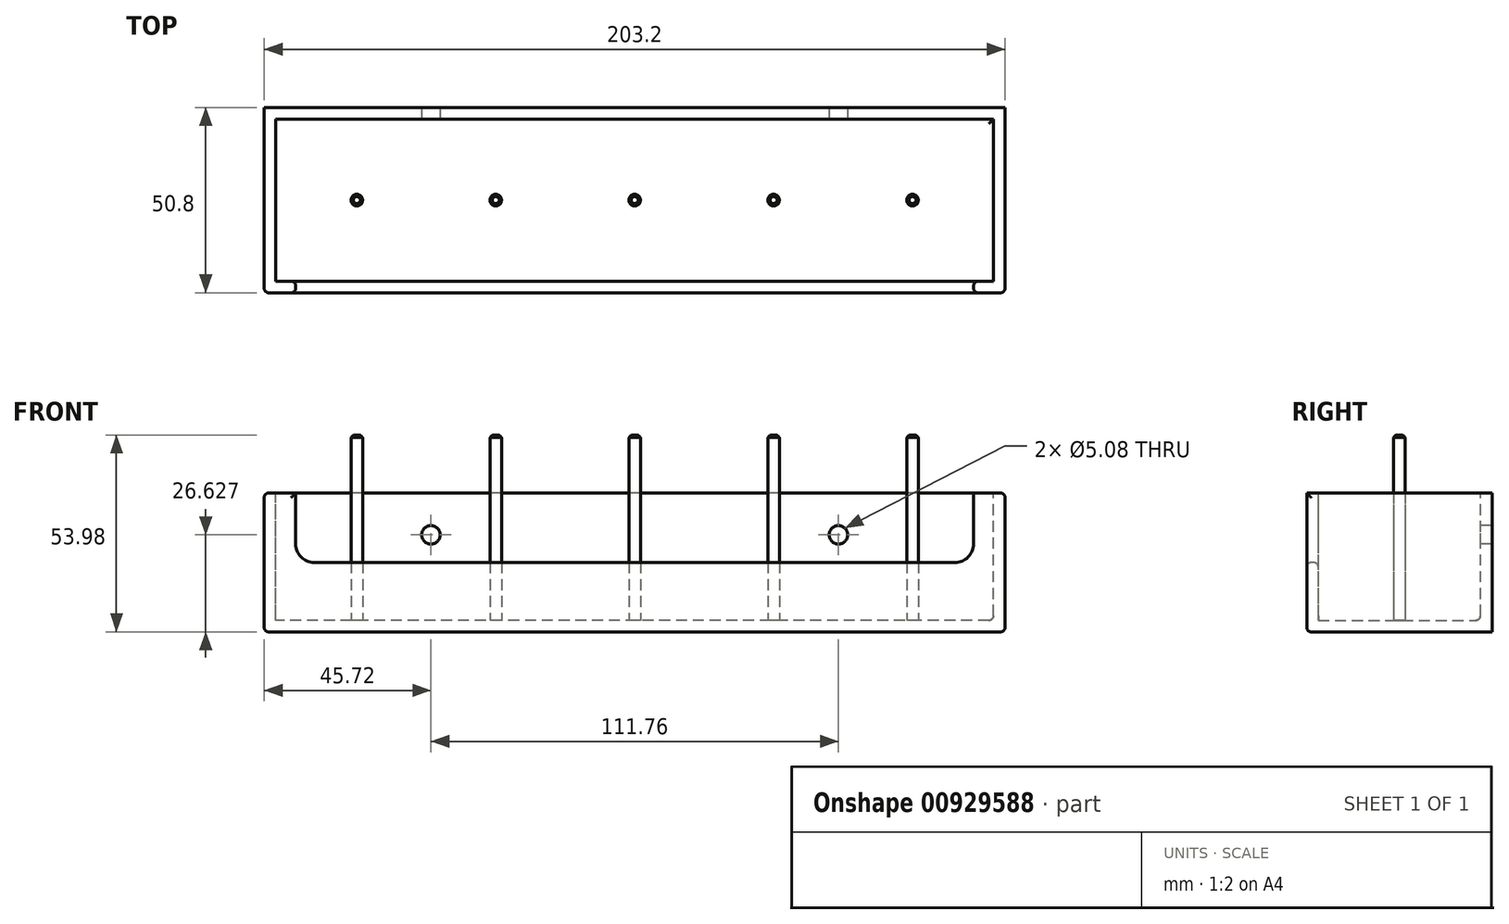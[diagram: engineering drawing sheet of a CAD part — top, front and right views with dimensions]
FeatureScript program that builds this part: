
annotation { "Feature Type Name" : "Feature", "Feature Type Description" : "" }
export const myFeature = defineFeature(function(context is Context, id is Id, definition is map)
    precondition{}
    {
        {
            var Q0;
            Q0=qCreatedBy(makeId("Front.planeOp"),FACE);
            var sketch = newSketch(context, id + "F0", { "sketchPlane" : qUnion([Q0])});
            skLineSegment(sketch, "E0.bottom", {"start": v(101.6, -19.05) * mm, "end": v(-101.6, -19.05) * mm});
            skLineSegment(sketch, "E0.top", {"start": v(101.6, 19.05) * mm, "end": v(-101.6, 19.05) * mm});
            skLineSegment(sketch, "E0.left", {"start": v(101.6, -19.05) * mm, "end": v(101.6, 19.05) * mm});
            skLineSegment(sketch, "E0.right", {"start": v(-101.6, -19.05) * mm, "end": v(-101.6, 19.05) * mm});
            skPoint(sketch, "E0.middle", {"position": v(0, 0) * mm});
            skSolve(sketch);
        }
        {
            var Q0;
            Q0 = qSketchRegion(id + "F0", true);
            extrude(context, id + "F1", {"entities" : qUnion([Q0]), "endBound" : BoundingType.SYMMETRIC, "depth" : 50.8 * mm, "offsetDistance" : 25.4 * mm});
        }
        {
            var Q0;
            Q0=makeQuery(id+"F1.opExtrude","SWEPT_FACE",FACE,{"disambiguationData":[OSD([sQuery(id+"F0.wireOp",EDGE,"E0.top")])]});
            var sketch = newSketch(context, id + "F2", { "sketchPlane" : qUnion([Q0])});
            skLineSegment(sketch, "E1.bottom", {"start": v(98.43, -22.22) * mm, "end": v(-98.43, -22.23) * mm});
            skLineSegment(sketch, "E1.top", {"start": v(98.43, 22.23) * mm, "end": v(-98.43, 22.22) * mm});
            skLineSegment(sketch, "E1.left", {"start": v(98.43, -22.22) * mm, "end": v(98.43, 22.23) * mm});
            skLineSegment(sketch, "E1.right", {"start": v(-98.43, -22.23) * mm, "end": v(-98.43, 22.22) * mm});
            skPoint(sketch, "E1.middle", {"position": v(0, 0) * mm});
            skSolve(sketch);
        }
        {
            var Q0;
            Q0=makeQuery(id+"F2.imprint","IMPRINT",FACE,{"disambiguationData":[TD([[makeQuery(id+"F2.imprint","IMPRINT",EDGE,{"derivedFrom":sQuery(id+"F2.wireOp",EDGE,"E1.bottom")}),-1.0]])]});
            extrude(context, id + "F3", {"entities" : qUnion([Q0]), "operationType" : NewBodyOperationType.REMOVE, "oppositeDirection" : true, "depth" : 34.92 * mm, "offsetDistance" : 25.4 * mm});
        }
        {
            var Q0;
            Q0=makeQuery(id+"F3.boolean.opBoolean","COPY",FACE,{"derivedFrom":makeQuery(id+"F3.opExtrude","CAP_FACE",FACE,{"disambiguationData":[OSD([sQuery(id+"F2.wireOp",EDGE,"E1.bottom"),sQuery(id+"F2.wireOp",EDGE,"E1.top"),sQuery(id+"F2.wireOp",EDGE,"E1.left"),sQuery(id+"F2.wireOp",EDGE,"E1.right")])],"isStart":false})});
            var sketch = newSketch(context, id + "F4", { "sketchPlane" : qUnion([Q0])});
            skCircle(sketch, "E2", {"center": v(0, 0) * mm, "radius": 1.59 * mm});
            skCircle(sketch, "E3", {"center": v(-38.1, 0) * mm, "radius": 1.59 * mm});
            skCircle(sketch, "E4", {"center": v(-76.2, 0) * mm, "radius": 1.59 * mm});
            skCircle(sketch, "E5", {"center": v(38.1, 0) * mm, "radius": 1.59 * mm});
            skCircle(sketch, "E6", {"center": v(76.2, 0) * mm, "radius": 1.59 * mm});
            skSolve(sketch);
        }
        {
            var Q0;
            Q0 = qSketchRegion(id + "F4", true);
            extrude(context, id + "F5", {"entities" : qUnion([Q0]), "operationType" : NewBodyOperationType.ADD, "depth" : 50.8 * mm, "offsetDistance" : 25.4 * mm});
        }
        {
            var Q0;
            Q0=makeQuery(id+"F1.opExtrude","SWEPT_FACE",FACE,{"disambiguationData":[OSD([sQuery(id+"F0.wireOp",EDGE,"E0.top")])]});
            var sketch = newSketch(context, id + "F6", { "sketchPlane" : qUnion([Q0])});
            skLineSegment(sketch, "E7.bottom", {"start": v(92.95, -18.89) * mm, "end": v(-92.95, -18.89) * mm});
            skLineSegment(sketch, "E7.top", {"start": v(92.95, -28.85) * mm, "end": v(-92.95, -28.85) * mm});
            skLineSegment(sketch, "E7.left", {"start": v(92.95, -18.89) * mm, "end": v(92.95, -28.85) * mm});
            skLineSegment(sketch, "E7.right", {"start": v(-92.95, -18.89) * mm, "end": v(-92.95, -28.85) * mm});
            skPoint(sketch, "E7.middle", {"position": v(0, -23.87) * mm});
            skPoint(sketch, "E7.middle.positionSnap0", {"position": v(0, -25.4) * mm});
            skPoint(sketch, "E7.centerSnap0", {"position": v(0, -25.4) * mm});
            skSolve(sketch);
        }
        {
            var Q0;
            Q0 = qSketchRegion(id + "F6", true);
            extrude(context, id + "F7", {"entities" : qUnion([Q0]), "operationType" : NewBodyOperationType.REMOVE, "oppositeDirection" : true, "depth" : 19.05 * mm, "offsetDistance" : 25.4 * mm});
        }
        {
            var Q0;
            Q0=makeQuery(id+"F7.boolean.opBoolean","COPY",EDGE,{"derivedFrom":makeQuery(id+"F7.opExtrude","CAP_EDGE",EDGE,{"disambiguationData":[OSD([sQuery(id+"F6.wireOp",EDGE,"E7.right")])],"isStart":true})});
            var Q1;
            Q1=makeQuery(id+"F7.boolean.opBoolean","COPY",EDGE,{"derivedFrom":makeQuery(id+"F7.opExtrude","CAP_EDGE",EDGE,{"disambiguationData":[OSD([sQuery(id+"F6.wireOp",EDGE,"E7.right")])],"isStart":false})});
            var Q2;
            Q2=makeQuery(id+"F7.boolean.opBoolean","COPY",EDGE,{"derivedFrom":makeQuery(id+"F7.opExtrude","CAP_EDGE",EDGE,{"disambiguationData":[OSD([sQuery(id+"F6.wireOp",EDGE,"E7.left")])],"isStart":true})});
            var Q3;
            Q3=makeQuery(id+"F7.boolean.opBoolean","COPY",EDGE,{"derivedFrom":makeQuery(id+"F7.opExtrude","CAP_EDGE",EDGE,{"disambiguationData":[OSD([sQuery(id+"F6.wireOp",EDGE,"E7.left")])],"isStart":false})});
            fillet(context, id + "F8", {"entities" : qUnion([Q0, Q1, Q2, Q3]), "radius" : 5.08 * mm, "tangentPropagation" : true, "allowEdgeOverflow" : false});
        }
        {
            var Q0;
            Q0=makeQuery(id+"F5.opExtrude","CAP_EDGE",EDGE,{"disambiguationData":[OSD([sQuery(id+"F4.wireOp",EDGE,"E2")])],"isStart":false});
            var Q1;
            Q1=makeQuery(id+"F5.opExtrude","CAP_EDGE",EDGE,{"disambiguationData":[OSD([sQuery(id+"F4.wireOp",EDGE,"E3")])],"isStart":false});
            var Q2;
            Q2=makeQuery(id+"F5.opExtrude","CAP_FACE",FACE,{"disambiguationData":[OSD([sQuery(id+"F4.wireOp",EDGE,"E5")])],"isStart":false});
            var Q3;
            Q3=makeQuery(id+"F5.opExtrude","CAP_EDGE",EDGE,{"disambiguationData":[OSD([sQuery(id+"F4.wireOp",EDGE,"E6")])],"isStart":false});
            var Q4;
            Q4=makeQuery(id+"F5.opExtrude","CAP_EDGE",EDGE,{"disambiguationData":[OSD([sQuery(id+"F4.wireOp",EDGE,"E4")])],"isStart":false});
            chamfer(context, id + "F9", {"entities" : qUnion([Q0, Q1, Q2, Q3, Q4]), "width" : 0.64 * mm, "tangentPropagation" : true});
        }
        {
            var Q0;
            Q0=makeQuery(id+"F3.boolean.opBoolean","COPY",EDGE,{"derivedFrom":makeQuery(id+"F3.opExtrude","CAP_EDGE",EDGE,{"disambiguationData":[OSD([sQuery(id+"F2.wireOp",EDGE,"E1.top")])],"isStart":true})});
            var Q1;
            Q1=makeQuery(id+"F3.boolean.opBoolean","COPY",EDGE,{"derivedFrom":makeQuery(id+"F3.opExtrude","CAP_EDGE",EDGE,{"disambiguationData":[OSD([sQuery(id+"F2.wireOp",EDGE,"E1.right")])],"isStart":true})});
            var Q2;
            Q2=makeQuery(id+"F7.boolean.opBoolean","INTERSECT",EDGE,{"derivedFrom":[makeQuery(id+"F1.opExtrude","CAP_FACE",FACE,{"disambiguationData":[OSD([sQuery(id+"F0.wireOp",EDGE,"E0.bottom"),sQuery(id+"F0.wireOp",EDGE,"E0.top"),sQuery(id+"F0.wireOp",EDGE,"E0.left"),sQuery(id+"F0.wireOp",EDGE,"E0.right")])],"isStart":false}),makeQuery(id+"F7.opExtrude","CAP_FACE",FACE,{"disambiguationData":[OSD([sQuery(id+"F6.wireOp",EDGE,"E7.bottom"),sQuery(id+"F6.wireOp",EDGE,"E7.top"),sQuery(id+"F6.wireOp",EDGE,"E7.left"),sQuery(id+"F6.wireOp",EDGE,"E7.right")])],"isStart":false})]});
            var Q3;
            Q3=makeQuery(id+"F8.opFillet","BLEND_EDGE",EDGE,{"blendedFrom":[makeQuery(id+"F7.boolean.opBoolean","COPY",EDGE,{"derivedFrom":makeQuery(id+"F7.opExtrude","CAP_EDGE",EDGE,{"disambiguationData":[OSD([sQuery(id+"F6.wireOp",EDGE,"E7.right")])],"isStart":false})}),makeQuery(id+"F1.opExtrude","CAP_FACE",FACE,{"disambiguationData":[OSD([sQuery(id+"F0.wireOp",EDGE,"E0.bottom"),sQuery(id+"F0.wireOp",EDGE,"E0.top"),sQuery(id+"F0.wireOp",EDGE,"E0.left"),sQuery(id+"F0.wireOp",EDGE,"E0.right")])],"isStart":false})],"blendedInto":[makeQuery(id+"F1.opExtrude","CAP_FACE",FACE,{"disambiguationData":[OSD([sQuery(id+"F0.wireOp",EDGE,"E0.bottom"),sQuery(id+"F0.wireOp",EDGE,"E0.top"),sQuery(id+"F0.wireOp",EDGE,"E0.left"),sQuery(id+"F0.wireOp",EDGE,"E0.right")])],"isStart":false})]});
            var Q4;
            Q4=makeQuery(id+"F7.boolean.opBoolean","INTERSECT",EDGE,{"derivedFrom":[makeQuery(id+"F1.opExtrude","CAP_FACE",FACE,{"disambiguationData":[OSD([sQuery(id+"F0.wireOp",EDGE,"E0.bottom"),sQuery(id+"F0.wireOp",EDGE,"E0.top"),sQuery(id+"F0.wireOp",EDGE,"E0.left"),sQuery(id+"F0.wireOp",EDGE,"E0.right")])],"isStart":false}),makeQuery(id+"F7.opExtrude","SWEPT_FACE",FACE,{"disambiguationData":[OSD([sQuery(id+"F6.wireOp",EDGE,"E7.right")])]})]});
            var Q5;
            {var subQ0=sQuery(id+"F0.wireOp",EDGE,"E0.right");var subQ1=sQuery(id+"F0.wireOp",EDGE,"E0.top");Q5=makeQuery(id+"F7.boolean.opBoolean","SPLIT",EDGE,{"disambiguationData":[TD([makeQuery(id+"F1.opExtrude","SWEPT_FACE",FACE,{"disambiguationData":[OSD([subQ0])]})])],"derivedFrom":makeQuery(id+"F1.opExtrude","CAP_EDGE",EDGE,{"disambiguationData":[OSD([subQ1])],"isStart":false})});}
            var Q6;
            Q6=makeQuery(id+"F1.opExtrude","SWEPT_EDGE",EDGE,{"disambiguationData":[OSD([sQuery(id+"F0.wireOp",EDGE,"E0.top"),sQuery(id+"F0.wireOp",EDGE,"E0.right")])]});
            var Q7;
            Q7=makeQuery(id+"F1.opExtrude","SWEPT_EDGE",EDGE,{"disambiguationData":[OSD([sQuery(id+"F0.wireOp",EDGE,"E0.top"),sQuery(id+"F0.wireOp",EDGE,"E0.left")])]});
            var Q8;
            Q8=makeQuery(id+"F1.opExtrude","CAP_EDGE",EDGE,{"disambiguationData":[OSD([sQuery(id+"F0.wireOp",EDGE,"E0.left")])],"isStart":false});
            var Q9;
            Q9=makeQuery(id+"F1.opExtrude","CAP_EDGE",EDGE,{"disambiguationData":[OSD([sQuery(id+"F0.wireOp",EDGE,"E0.bottom")])],"isStart":false});
            var Q10;
            Q10=makeQuery(id+"F1.opExtrude","SWEPT_EDGE",EDGE,{"disambiguationData":[OSD([sQuery(id+"F0.wireOp",EDGE,"E0.bottom"),sQuery(id+"F0.wireOp",EDGE,"E0.left")])]});
            var Q11;
            Q11=makeQuery(id+"F1.opExtrude","CAP_EDGE",EDGE,{"disambiguationData":[OSD([sQuery(id+"F0.wireOp",EDGE,"E0.right")])],"isStart":false});
            var Q12;
            Q12=makeQuery(id+"F1.opExtrude","SWEPT_EDGE",EDGE,{"disambiguationData":[OSD([sQuery(id+"F0.wireOp",EDGE,"E0.bottom"),sQuery(id+"F0.wireOp",EDGE,"E0.right")])]});
            var Q13;
            Q13=makeQuery(id+"F3.boolean.opBoolean","COPY",EDGE,{"derivedFrom":makeQuery(id+"F3.opExtrude","CAP_EDGE",EDGE,{"disambiguationData":[OSD([sQuery(id+"F2.wireOp",EDGE,"E1.top")])],"isStart":false})});
            var Q14;
            Q14=makeQuery(id+"F7.boolean.opBoolean","INTERSECT",EDGE,{"derivedFrom":[makeQuery(id+"F3.boolean.opBoolean","COPY",FACE,{"derivedFrom":makeQuery(id+"F3.opExtrude","SWEPT_FACE",FACE,{"disambiguationData":[OSD([sQuery(id+"F2.wireOp",EDGE,"E1.bottom")])]})}),makeQuery(id+"F7.opExtrude","CAP_FACE",FACE,{"disambiguationData":[OSD([sQuery(id+"F6.wireOp",EDGE,"E7.bottom"),sQuery(id+"F6.wireOp",EDGE,"E7.top"),sQuery(id+"F6.wireOp",EDGE,"E7.left"),sQuery(id+"F6.wireOp",EDGE,"E7.right")])],"isStart":false})]});
            var Q15;
            Q15=makeQuery(id+"F3.boolean.opBoolean","COPY",EDGE,{"derivedFrom":makeQuery(id+"F3.opExtrude","CAP_EDGE",EDGE,{"disambiguationData":[OSD([sQuery(id+"F2.wireOp",EDGE,"E1.left")])],"isStart":true})});
            var Q16;
            Q16=makeQuery(id+"F3.boolean.opBoolean","COPY",EDGE,{"derivedFrom":makeQuery(id+"F3.opExtrude","CAP_EDGE",EDGE,{"disambiguationData":[OSD([sQuery(id+"F2.wireOp",EDGE,"E1.left")])],"isStart":false})});
            fillet(context, id + "F10", {"entities" : qUnion([Q0, Q1, Q2, Q3, Q4, Q5, Q6, Q7, Q8, Q9, Q10, Q11, Q12, Q13, Q14, Q15, Q16]), "radius" : 1.27 * mm, "tangentPropagation" : true, "allowEdgeOverflow" : false});
        }
        {
            var Q0;
            Q0=makeQuery(id+"F3.boolean.opBoolean","COPY",FACE,{"derivedFrom":makeQuery(id+"F3.opExtrude","SWEPT_FACE",FACE,{"disambiguationData":[OSD([sQuery(id+"F2.wireOp",EDGE,"E1.top")])]})});
            var sketch = newSketch(context, id + "F11", { "sketchPlane" : qUnion([Q0])});
            skCircle(sketch, "E8", {"center": v(55.88, 7.58) * mm, "radius": 2.54 * mm});
            skCircle(sketch, "E9", {"center": v(-55.88, 7.58) * mm, "radius": 2.54 * mm});
            skSolve(sketch);
        }
        {
            var Q0;
            Q0 = qSketchRegion(id + "F11", true);
            extrude(context, id + "F12", {"entities" : qUnion([Q0]), "operationType" : NewBodyOperationType.REMOVE, "oppositeDirection" : true, "depth" : 5.08 * mm, "offsetDistance" : 25.4 * mm});
        }
    });
